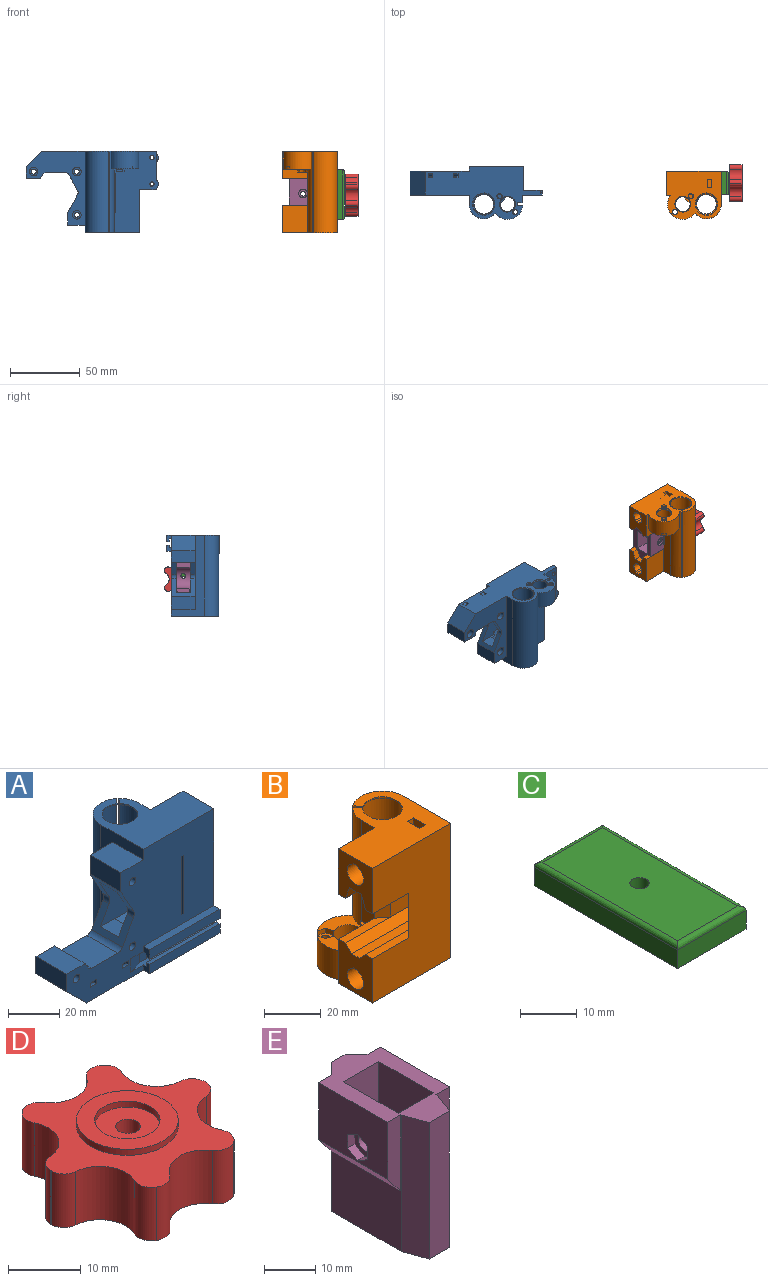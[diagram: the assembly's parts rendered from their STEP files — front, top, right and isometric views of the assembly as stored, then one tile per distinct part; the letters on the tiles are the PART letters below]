
ASSEMBLY  parts=5 mates=4
PART A: 160 faces, bbox 95x38x58 mm
  f0: plane 12.5x7.8mm, normal (1,0,0), area 61.7mm2, adj f1,f4,f8,f146,f148,f149
  f1: plane 19.74x17.5mm, normal (0,0,1), area 118mm2, adj f0,f8,f15,f16,f92,f98,f99,f100
  f2: plane 81.5x58mm, normal (0,-1,0), area 2689.5mm2, adj f3,f4,f30,f31,f32,f33,f34,f35
  f3: plane 58x20.5mm, normal (1,0,0), area 534.3mm2, adj f2,f4,f8,f26,f27,f28,f29,f44
  f4: plane 82.55x38mm, normal (0,0,-1), area 1612.4mm2, adj f0,f2,f3,f8,f16,f23,f43,f45
  f5: plane 2.33x1.17mm, normal (0,0,-1), area 0.6mm2, adj f12,f112,f120
  f6: plane 2.33x1.17mm, normal (0,0,-1), area 0.6mm2, adj f107,f112,f120
  f7: plane 2.33x1.17mm, normal (0,0,-1), area 0.6mm2, adj f107,f110,f120
  f8: plane 58x31.5mm, normal (0,1,0), area 1132.1mm2, adj f0,f1,f3,f4,f9,f44,f48,f49
  f9: plane 45x13.07mm, normal (1,0,0), area 391.3mm2, adj f8,f11,f16,f44,f48,f50,f64,f65
  f10: plane 4.64x4.64mm, normal (0,0,1), area 5.1mm2, adj f105,f114
  f11: plane 0.06x0.03mm, normal (0,0,1), area 0mm2, adj f9,f115,f116
  f12: plane 3.96x3.96mm, normal (0.71,0.71,0), area 4.5mm2, adj f5,f13,f14,f19,f109,f110,f111,f112
  f13: plane 2.33x1.17mm, normal (0,0,-1), area 0.6mm2, adj f12,f110,f120
  f14: plane 3.96x3.96mm, normal (0.71,-0.71,0), area 18.4mm2, adj f12,f18,f95,f96,f106,f107,f109,f111
  f15: cylinder r=5.25mm len=11.6mm, axis (0,0,-1), area 357mm2, adj f1,f17,f18,f94,f95,f97,f102,f103
  f16: cylinder r=10.5mm len=58mm, axis (0,0,-1), area 1765.4mm2, adj f1,f4,f9,f43,f44,f89,f90,f91
  f17: plane 3x0.78mm, normal (-0.53,0.85,0), area 2.8mm2, adj f15,f19,f95,f106
  f18: plane 3x0.78mm, normal (0.85,-0.53,0), area 2.8mm2, adj f14,f15,f95,f106
  f19: plane 3.96x3.96mm, normal (-0.71,0.71,0), area 18.5mm2, adj f12,f17,f95,f96,f106,f107,f109,f113
  f20: cylinder r=1.65mm len=9.5mm, axis (0,0,-1), area 98.5mm2, adj f97,f123
  f21: cylinder r=7.5mm len=56.85mm, axis (0,0,-1), area 2622.3mm2, adj f22,f87,f89,f90,f91
  f22: cone r=7.5mm half-angle=63.4deg, axis (0,0,-1), area 24.9mm2, adj f21,f88,f89,f90
  f23: plane 53x42.5mm, normal (0,1,0), area 903.5mm2, adj f4,f24,f35,f36,f37,f38,f40,f41
  f24: cylinder r=3.5mm len=3.5mm, axis (0,-1,0), area 12.4mm2, adj f23,f38,f40,f65
  f25: plane 10x3.25mm, normal (1,0,0), area 23.1mm2, adj f48,f64,f65,f68,f69,f84
  f26: plane 30.15x0.91mm, normal (0,0.71,-0.71), area 36.2mm2, adj f3,f27,f29,f80,f81
  f27: cylinder r=4.07mm len=29.1mm, axis (1,0,0), area 618.8mm2, adj f3,f26,f28,f81
  f28: plane 30.15x0.91mm, normal (0,-0.71,-0.71), area 36.2mm2, adj f3,f27,f29,f80,f81
  f29: plane 30.11x2.39mm, normal (0,0,-1), area 70.9mm2, adj f3,f26,f28,f80
  f30: plane 28x6.57mm, normal (1,0,0), area 108.5mm2, adj f2,f48,f50,f67,f68,f69
  f31: plane 28x6.57mm, normal (-1,0,0), area 108.5mm2, adj f2,f48,f50,f58,f59,f60
  f32: cylinder r=1.8mm len=13.5mm, axis (0,-1,0), area 152.7mm2, adj f2,f57
  f33: cylinder r=1.8mm len=13.5mm, axis (0,-1,0), area 152.7mm2, adj f2,f55
  f34: cylinder r=1.8mm len=13.5mm, axis (0,-1,0), area 152.7mm2, adj f2,f53
  f35: plane 17x1.73mm, normal (0.5,0,0.87), area 34mm2, adj f2,f23,f36,f51
  f36: plane 17x14.58mm, normal (0,0,1), area 247.8mm2, adj f2,f23,f35,f37
  f37: cylinder r=3mm len=17mm, axis (0,-1,0), area 54.2mm2, adj f2,f23,f36,f38
  f38: plane 17x11.05mm, normal (-0.87,0,0.49), area 116.3mm2, adj f2,f23,f24,f37,f39,f65,f68,f84
  f39: cylinder r=3.5mm len=3.5mm, axis (0,-1,0), area 12.4mm2, adj f2,f38,f40,f68
  f40: plane 17x12.59mm, normal (-0.87,0,-0.49), area 132.8mm2, adj f2,f23,f24,f39,f41,f65,f68,f85
  f41: plane 17x9.14mm, normal (-1,0,0), area 155.4mm2, adj f2,f23,f40,f42
  f42: plane 17x12.5mm, normal (0,0,1), area 212.5mm2, adj f2,f23,f41,f43
  f43: plane 58x23.5mm, normal (-1,0,0), area 462mm2, adj f2,f4,f16,f23,f42,f44
  f44: plane 39x34mm, normal (0,0,1), area 815.2mm2, adj f2,f3,f8,f9,f16,f43,f88,f89
  f45: plane 17x10.95mm, normal (-0.71,0,-0.71), area 263.3mm2, adj f2,f4,f23,f46
  f46: plane 17x8.3mm, normal (-1,0,0), area 141.1mm2, adj f2,f23,f45,f47
  f47: plane 17x10.21mm, normal (0,0,1), area 173.6mm2, adj f2,f23,f46,f51
  f48: plane 41.5x17mm, normal (0,0,1), area 173.3mm2, adj f2,f3,f8,f9,f25,f30,f31,f49
  f49: plane 28x6.57mm, normal (-1,0,0), area 108.5mm2, adj f8,f48,f50,f61,f62,f63
  f50: plane 41.5x17mm, normal (0,0,-1), area 256.4mm2, adj f2,f3,f8,f9,f30,f31,f49,f60
  f51: plane 17x2.97mm, normal (0.87,0,0.5), area 58.3mm2, adj f2,f23,f35,f47
  f52: cylinder r=3.1mm len=6.2mm, axis (0,1,0), area 68.2mm2, adj f23,f53
  f53: plane 6.2x6.2mm, normal (0,1,0), area 20mm2, adj f34,f52
  f54: cylinder r=3.1mm len=6.2mm, axis (0,1,0), area 68.2mm2, adj f23,f55
  f55: plane 6.2x6.2mm, normal (0,1,0), area 20mm2, adj f33,f54
  f56: cylinder r=3.1mm len=6.2mm, axis (0,1,0), area 68.2mm2, adj f23,f57
  f57: plane 6.2x6.2mm, normal (0,1,0), area 20mm2, adj f32,f56
  f58: plane 17x3.07mm, normal (0,0.71,0.71), area 73.8mm2, adj f3,f31,f48,f59
  f59: plane 19.31x17mm, normal (0,1,0), area 328.3mm2, adj f3,f31,f58,f60
  f60: plane 17x5.62mm, normal (0,0.94,-0.34), area 101.7mm2, adj f3,f31,f50,f59
  f61: plane 17x5.62mm, normal (0,-0.94,-0.34), area 101.7mm2, adj f3,f49,f50,f62
  f62: plane 38.38x30.5mm, normal (0,-1,0), area 659.9mm2, adj f3,f4,f49,f61,f63,f150,f151,f152
  f63: plane 17x3.07mm, normal (0,-0.71,0.71), area 73.8mm2, adj f3,f48,f49,f62
  f64: plane 23.5x3.07mm, normal (0,-0.71,0.71), area 102mm2, adj f9,f25,f48,f65
  f65: plane 31.95x22mm, normal (0,-1,0), area 573.5mm2, adj f9,f24,f25,f38,f40,f64,f66,f83
  f66: plane 23.5x5.62mm, normal (0,-0.94,-0.34), area 131.9mm2, adj f9,f50,f65,f70,f83,f85
  f67: plane 23.5x5.62mm, normal (0,0.94,-0.34), area 131.9mm2, adj f30,f50,f68,f70,f85,f86
  f68: plane 31.95x22mm, normal (0,1,0), area 573.5mm2, adj f25,f30,f38,f39,f40,f67,f69,f84
  f69: plane 23.5x3.07mm, normal (0,0.71,0.71), area 102mm2, adj f25,f30,f48,f68
  f70: plane 8.04x2.93mm, normal (1,0,0), area 20.4mm2, adj f50,f66,f67,f85
  f71: plane 30.15x0.91mm, normal (0,0.71,-0.71), area 36.2mm2, adj f3,f72,f74,f76,f77
  f72: cylinder r=4.07mm len=29.1mm, axis (1,0,0), area 618.8mm2, adj f3,f71,f73,f77
  f73: plane 30.15x0.91mm, normal (0,-0.71,-0.71), area 36.2mm2, adj f3,f72,f74,f76,f77
  f74: plane 30.11x2.39mm, normal (0,0,-1), area 70.9mm2, adj f3,f71,f73,f76
  f75: cylinder r=5mm len=10mm, axis (-1,0,0), area 157.1mm2, adj f76,f78
  f76: cone r=5mm half-angle=13.6deg, axis (-1,0,0), area 85.3mm2, adj f71,f73,f74,f75,f77
  f77: plane 8.6x8.3mm, normal (-1,0,0), area 5.1mm2, adj f71,f72,f73,f76
  f78: plane 10x10mm, normal (1,0,0), area 78.5mm2, adj f75
  f79: cylinder r=5mm len=10mm, axis (1,0,0), area 157.1mm2, adj f80,f82
  f80: cone r=5mm half-angle=13.6deg, axis (-1,0,0), area 85.3mm2, adj f26,f28,f29,f79,f81
  f81: plane 8.6x8.3mm, normal (-1,0,0), area 5.1mm2, adj f26,f27,f28,f80
  f82: plane 10x10mm, normal (1,0,0), area 78.5mm2, adj f79
  f83: plane 2.69x0.98mm, normal (-1,0,0), area 1.3mm2, adj f65,f66,f85
  f84: plane 10x7.79mm, normal (0,0,1), area 77.9mm2, adj f25,f38,f65,f68
  f85: plane 11.45x10mm, normal (0,0,-1), area 90.3mm2, adj f40,f65,f66,f67,f68,f70,f83,f86
  f86: plane 2.69x0.98mm, normal (-1,0,0), area 1.3mm2, adj f67,f68,f85
  f87: cone r=7.5mm half-angle=59deg, axis (0,0,-1), area 28.4mm2, adj f4,f21
  f88: cylinder r=7mm len=14mm, axis (0,0,1), area 25.8mm2, adj f22,f44,f89,f90
  f89: plane 57.5x2.69mm, normal (-0.77,0.64,0), area 173.1mm2, adj f16,f21,f22,f44,f88,f91
  f90: plane 57.5x2.69mm, normal (0.77,-0.64,0), area 173.1mm2, adj f16,f21,f22,f44,f88,f91
  f91: plane 2.94x2.7mm, normal (0,0,1), area 3mm2, adj f16,f21,f89,f90
  f92: cylinder r=11mm len=19.74mm, axis (0,0,-1), area 327.5mm2, adj f1,f4,f16,f146
  f93: cylinder r=1.65mm len=8mm, axis (0,0,-1), area 82.9mm2, adj f95,f122
  f94: cone r=5.25mm half-angle=26.6deg, axis (0,0,-1), area 34.6mm2, adj f4,f15
  f95: plane 8.7x8.7mm, normal (0,0,1), area 24.1mm2, adj f14,f15,f17,f18,f19,f93,f96
  f96: plane 3.96x3.96mm, normal (0.71,0.71,0), area 16.8mm2, adj f14,f19,f95,f109
  f97: plane 6.25x6.25mm, normal (0,0,1), area 18.6mm2, adj f15,f20,f98,f99,f100,f101,f102,f103
  f98: plane 3.12x2mm, normal (-0.97,0.26,0), area 6.5mm2, adj f1,f97,f99,f104
  f99: plane 2.29x2.29mm, normal (-0.71,-0.71,0), area 6.5mm2, adj f1,f97,f98,f100
  f100: plane 3.12x2mm, normal (0.26,-0.97,0), area 6.5mm2, adj f1,f97,f99,f101
  f101: plane 3.12x2mm, normal (0.97,-0.26,0), area 6.5mm2, adj f1,f97,f100,f103
  f102: plane 2x0.63mm, normal (0.71,0.71,0), area 1.8mm2, adj f1,f15,f97,f104
  f103: plane 2x0.63mm, normal (0.71,0.71,0), area 1.8mm2, adj f1,f15,f97,f101
  f104: plane 3.12x2mm, normal (-0.26,0.97,0), area 6.5mm2, adj f1,f97,f98,f102
  f105: plane 7.23x7.23mm, normal (0.71,0.71,0), area 13.9mm2, adj f1,f8,f10,f15,f16,f106,f114,f119
  f106: plane 5.89x5.89mm, normal (0,0,-1), area 12.9mm2, adj f14,f15,f17,f18,f19,f105,f107
  f107: plane 3.96x3.96mm, normal (-0.71,-0.71,0), area 4.5mm2, adj f6,f7,f14,f19,f106,f110,f111,f112
  f108: plane 0.06x0.03mm, normal (0,0,1), area 0mm2, adj f8,f117,f118
  f109: plane 4.77x4.77mm, normal (0,0,-1), area 6.4mm2, adj f12,f14,f19,f96
  f110: plane 2.33x2.33mm, normal (0.71,-0.71,0), area 1.6mm2, adj f7,f12,f13,f107,f111
  f111: plane 3.15x3.15mm, normal (0,0,-1), area 3.8mm2, adj f12,f14,f107,f110
  f112: plane 2.33x2.33mm, normal (-0.71,0.71,0), area 1.7mm2, adj f5,f6,f12,f107,f113
  f113: plane 3.15x3.15mm, normal (0,0,-1), area 3.8mm2, adj f12,f19,f107,f112
  f114: cylinder r=5.25mm len=4.64mm, axis (0,0,-1), area 10.6mm2, adj f10,f105,f119
  f115: plane 1.5x0.03mm, normal (-0.71,-0.71,0), area 0.1mm2, adj f9,f11,f116,f119
  f116: plane 1.5x0.03mm, normal (-0.71,0.71,0), area 0.1mm2, adj f9,f11,f115,f119
  f117: plane 1.5x0.03mm, normal (0.71,-0.71,0), area 0.1mm2, adj f8,f108,f118,f119
  f118: plane 1.5x0.03mm, normal (-0.71,-0.71,0), area 0.1mm2, adj f8,f108,f117,f119
  f119: plane 7.23x7.23mm, normal (0,0,1), area 20.8mm2, adj f8,f9,f16,f105,f114,f115,f116,f117
  f120: cylinder r=1.65mm len=3.3mm, axis (0,0,-1), area 10.4mm2, adj f5,f6,f7,f13,f121
  f121: plane 3.3x3.3mm, normal (0,0,-1), area 8.6mm2, adj f120
  f122: cone r=1.65mm half-angle=15.4deg, axis (0,0,-1), area 11.6mm2, adj f4,f93
  f123: cone r=1.65mm half-angle=15.4deg, axis (0,0,-1), area 11.6mm2, adj f4,f20
  f124: plane 4.5x3.5mm, normal (-1,0,0), area 12.8mm2, adj f2,f4,f125,f126,f127,f128
  f125: plane 46x3.8mm, normal (0,0,1), area 155.2mm2, adj f2,f3,f124,f126,f135,f136,f137
  f126: plane 39x2mm, normal (0,1,0), area 78mm2, adj f3,f124,f125,f127
  f127: plane 39x2mm, normal (0,0,1), area 78mm2, adj f3,f124,f126,f128
  f128: plane 39x4.5mm, normal (0,-1,0), area 175.5mm2, adj f3,f4,f124,f127
  f129: plane 4.5x3.5mm, normal (-1,0,0), area 12.8mm2, adj f2,f130,f131,f132,f133,f134
  f130: plane 39x3.5mm, normal (0,0,1), area 136.5mm2, adj f2,f3,f129,f131
  f131: plane 39x4.5mm, normal (0,-1,0), area 175.5mm2, adj f3,f129,f130,f132
  f132: plane 39x2mm, normal (0,0,-1), area 78mm2, adj f3,f129,f131,f133
  f133: plane 39x2mm, normal (0,1,0), area 78mm2, adj f3,f129,f132,f134
  f134: plane 46x3.8mm, normal (0,0,-1), area 155.2mm2, adj f2,f3,f129,f133,f135,f136,f137
  f135: plane 6.5x0.3mm, normal (1,0,0), area 2mm2, adj f125,f134,f136,f137
  f136: plane 39x6.5mm, normal (0,-1,0), area 253.5mm2, adj f3,f125,f134,f135
  f137: plane 7x6.5mm, normal (0.27,-0.96,0), area 47.3mm2, adj f2,f125,f134,f135
  f138: plane 8.6x5.5mm, normal (-1,0,0), area 21.1mm2, adj f2,f4,f139,f141
  f139: cylinder r=3.5mm len=6.6mm, axis (1,0,0), area 32.6mm2, adj f2,f4,f138,f140
  f140: plane 8.6x5.5mm, normal (1,0,0), area 21.1mm2, adj f2,f4,f139,f141
  f141: cylinder r=5.5mm len=8.6mm, axis (1,0,0), area 41.8mm2, adj f2,f4,f138,f140
  f142: cylinder r=3.5mm len=6.6mm, axis (1,0,0), area 32.6mm2, adj f2,f4,f143,f145
  f143: plane 8.6x5.5mm, normal (1,0,0), area 21.1mm2, adj f2,f4,f142,f144
  f144: cylinder r=5.5mm len=8.6mm, axis (1,0,0), area 41.8mm2, adj f2,f4,f143,f145
  f145: plane 8.6x5.5mm, normal (-1,0,0), area 21.1mm2, adj f2,f4,f142,f144
  f146: plane 12.5x3.92mm, normal (0,-1,0), area 49mm2, adj f0,f1,f4,f92
  f147: plane 6.5x5.5mm, normal (1,0,0), area 35.8mm2, adj f4,f8,f148,f149
  f148: plane 5.5x3.5mm, normal (0,0,1), area 19.2mm2, adj f0,f8,f147,f149
  f149: plane 6.5x3.5mm, normal (0,1,0), area 22.7mm2, adj f0,f4,f147,f148
  f150: plane 20.15x3.5mm, normal (1,0,0), area 60.4mm2, adj f4,f8,f62,f151,f155,f157
  f151: cylinder r=4.5mm len=6.71mm, axis (0,1,0), area 11.4mm2, adj f62,f150,f157
  f152: plane 12x3.5mm, normal (0,0,1), area 42mm2, adj f3,f8,f62,f153
  f153: plane 3.5x0.65mm, normal (1,0,0), area 2.3mm2, adj f8,f62,f152,f155
  f154: cylinder r=1.4mm len=3.35mm, axis (0,1,0), area 29.5mm2, adj f62,f158
  f155: cylinder r=4.5mm len=6.71mm, axis (0,1,0), area 26.5mm2, adj f8,f62,f150,f153
  f156: cylinder r=1.4mm len=3.35mm, axis (0,1,0), area 29.5mm2, adj f62,f159
  f157: plane 6.71x1.5mm, normal (0,1,0), area 7mm2, adj f150,f151
  f158: cone r=1.4mm half-angle=45deg, axis (0,1,0), area 2mm2, adj f8,f154
  f159: cone r=1.55mm half-angle=45deg, axis (0,1,0), area 2mm2, adj f8,f156
PART B: 111 faces, bbox 39x34.5x58 mm
  f0: plane 2.33x1.17mm, normal (0,0,-1), area 0.6mm2, adj f4,f99,f107
  f1: plane 2.33x1.17mm, normal (0,0,-1), area 0.6mm2, adj f4,f97,f107
  f2: plane 2.33x1.17mm, normal (0,0,-1), area 0.6mm2, adj f95,f97,f107
  f3: plane 2.33x1.17mm, normal (0,0,-1), area 0.6mm2, adj f95,f99,f107
  f4: plane 3.96x3.96mm, normal (-0.71,0.71,0), area 4.5mm2, adj f0,f1,f5,f11,f96,f97,f98,f99
  f5: plane 3.96x3.96mm, normal (0.71,0.71,0), area 18.5mm2, adj f4,f10,f82,f83,f94,f95,f96,f100
  f6: cylinder r=5.25mm len=11.6mm, axis (0,0,-1), area 357mm2, adj f7,f10,f12,f81,f82,f84,f90,f91
  f7: plane 19.82x17.5mm, normal (0,0,1), area 144.7mm2, adj f6,f8,f9,f80,f85,f86,f87,f88
  f8: plane 19.07x18mm, normal (0,1,0), area 136.7mm2, adj f7,f13,f27,f36,f66,f80,f92,f101
  f9: cylinder r=10.5mm len=58mm, axis (0,0,1), area 1765.4mm2, adj f7,f13,f33,f36,f38,f77,f78,f79
  f10: plane 3x0.78mm, normal (0.53,0.85,0), area 2.8mm2, adj f5,f6,f82,f94
  f11: plane 3.96x3.96mm, normal (-0.71,-0.71,0), area 18.4mm2, adj f4,f12,f82,f83,f94,f95,f96,f98
  f12: plane 3x0.78mm, normal (-0.85,-0.53,0), area 2.8mm2, adj f6,f11,f82,f94
  f13: plane 43.5x6.5mm, normal (-1,0,0), area 282.8mm2, adj f8,f9,f26,f38,f67,f101
  f14: cylinder r=7mm len=14mm, axis (0,0,1), area 25.8mm2, adj f38,f40,f78,f79
  f15: cylinder r=1.7mm len=3.4mm, axis (1,0,0), area 16mm2, adj f44,f73
  f16: plane 20.02x0.89mm, normal (0,0.71,-0.71), area 24.3mm2, adj f17,f19,f31,f61,f74,f76
  f17: plane 20x2.39mm, normal (0,0,-1), area 47.6mm2, adj f16,f18,f20,f31,f61,f74
  f18: plane 20.02x0.89mm, normal (0,-0.71,-0.71), area 24.3mm2, adj f17,f19,f20,f31,f74,f76
  f19: cylinder r=4.07mm len=19.6mm, axis (-1,0,0), area 416.8mm2, adj f16,f18,f31,f76
  f20: plane 0.46x0.12mm, normal (-1,0,0), area 0mm2, adj f17,f18,f74
  f21: cylinder r=4.07mm len=19.6mm, axis (-1,0,0), area 416.8mm2, adj f22,f24,f27,f69
  f22: plane 20.02x0.89mm, normal (0,0.71,-0.71), area 24.3mm2, adj f21,f23,f27,f62,f69,f72
  f23: plane 20x2.39mm, normal (0,0,-1), area 47.6mm2, adj f22,f24,f25,f27,f62,f72
  f24: plane 20.02x0.89mm, normal (0,-0.71,-0.71), area 24.3mm2, adj f21,f23,f25,f27,f69,f72
  f25: plane 0.46x0.12mm, normal (-1,0,0), area 0mm2, adj f23,f24,f72
  f26: plane 19.62x18mm, normal (0,1,0), area 353.1mm2, adj f13,f31,f38,f65
  f27: plane 19.07x17mm, normal (-1,0,0), area 249.5mm2, adj f8,f21,f22,f23,f24,f28,f36,f51
  f28: plane 58x39mm, normal (0,-1,0), area 1914.4mm2, adj f27,f31,f33,f36,f38,f63,f64,f68
  f29: plane 19.31x16.5mm, normal (0,-1,0), area 318.6mm2, adj f33,f52,f53,f67
  f30: plane 19.31x16.5mm, normal (0,1,0), area 318.6mm2, adj f33,f55,f56,f68
  f31: plane 19.62x17mm, normal (-1,0,0), area 235.4mm2, adj f16,f17,f18,f19,f26,f28,f38,f53
  f32: cylinder r=1.7mm len=3.4mm, axis (1,0,0), area 16mm2, adj f48,f71
  f33: plane 58x23.5mm, normal (1,0,0), area 1047.4mm2, adj f9,f28,f29,f30,f36,f38,f51,f52
  f34: cylinder r=1.7mm len=4mm, axis (1,0,0), area 42.7mm2, adj f46,f60
  f35: cylinder r=1.7mm len=4mm, axis (1,0,0), area 42.7mm2, adj f42,f58
  f36: plane 39x34.5mm, normal (0,0,-1), area 907.5mm2, adj f8,f9,f27,f28,f33,f39,f46,f47
  f37: cylinder r=7.5mm len=56.85mm, axis (0,0,1), area 2622.3mm2, adj f39,f40,f77,f78,f79
  f38: plane 39x34mm, normal (0,0,1), area 797.2mm2, adj f9,f13,f14,f26,f28,f31,f33,f41
  f39: cone r=8mm half-angle=59deg, axis (0,0,-1), area 28.4mm2, adj f36,f37
  f40: cone r=7.5mm half-angle=63.4deg, axis (0,0,-1), area 24.9mm2, adj f14,f37,f78,f79
  f41: plane 10.6x3mm, normal (0,-1,0), area 31.8mm2, adj f38,f42,f44,f45
  f42: plane 10.6x6mm, normal (-1,0,0), area 54.5mm2, adj f35,f38,f41,f43,f45
  f43: plane 10.6x3mm, normal (0,1,0), area 31.8mm2, adj f38,f42,f44,f45
  f44: plane 10.6x6mm, normal (1,0,0), area 54.5mm2, adj f15,f38,f41,f43,f45
  f45: plane 6x3mm, normal (0,0,1), area 18mm2, adj f41,f42,f43,f44
  f46: plane 9.1x6mm, normal (-1,0,0), area 45.5mm2, adj f34,f36,f47,f49,f50
  f47: plane 9.1x3mm, normal (0,1,0), area 27.3mm2, adj f36,f46,f48,f50
  f48: plane 9.1x6mm, normal (1,0,0), area 45.5mm2, adj f32,f36,f47,f49,f50
  f49: plane 9.1x3mm, normal (0,-1,0), area 27.3mm2, adj f36,f46,f48,f50
  f50: plane 6x3mm, normal (0,0,-1), area 18mm2, adj f46,f47,f48,f49
  f51: plane 39x3.86mm, normal (0,0,1), area 150.5mm2, adj f27,f33,f52,f56
  f52: plane 39x3.07mm, normal (0,-0.71,0.71), area 169.4mm2, adj f27,f29,f33,f51,f66
  f53: plane 39x5.62mm, normal (0,-0.94,-0.34), area 233.2mm2, adj f29,f31,f33,f54,f65
  f54: plane 39x5.91mm, normal (0,0,-1), area 230.5mm2, adj f31,f33,f53,f55
  f55: plane 39x5.62mm, normal (0,0.94,-0.34), area 233.2mm2, adj f30,f31,f33,f54,f64
  f56: plane 39x3.07mm, normal (0,0.71,0.71), area 169.4mm2, adj f27,f30,f33,f51,f63
  f57: cylinder r=3mm len=6mm, axis (1,0,0), area 56.5mm2, adj f33,f58
  f58: plane 6x6mm, normal (1,0,0), area 19.2mm2, adj f35,f57
  f59: cylinder r=3mm len=6mm, axis (1,0,0), area 56.5mm2, adj f33,f60
  f60: plane 6x6mm, normal (1,0,0), area 19.2mm2, adj f34,f59
  f61: plane 0.46x0.12mm, normal (-1,0,0), area 0mm2, adj f16,f17,f74
  f62: plane 0.46x0.12mm, normal (-1,0,0), area 0mm2, adj f22,f23,f72
  f63: plane 22.5x3.5mm, normal (0,0,1), area 70.9mm2, adj f27,f28,f56,f68
  f64: plane 22.5x3.5mm, normal (0,0,-1), area 70.9mm2, adj f28,f31,f55,f68
  f65: plane 22.5x3.5mm, normal (0,0,-1), area 70.9mm2, adj f26,f31,f53,f67
  f66: plane 22.5x3.5mm, normal (0,0,1), area 70.9mm2, adj f8,f27,f52,f67
  f67: plane 19.31x4.5mm, normal (-0.61,-0.79,0), area 110.1mm2, adj f13,f29,f65,f66
  f68: plane 19.31x4.5mm, normal (-0.61,0.79,0), area 110.1mm2, adj f28,f30,f63,f64
  f69: plane 8.6x8.3mm, normal (1,0,0), area 5.1mm2, adj f21,f22,f24,f72
  f70: cylinder r=5.5mm len=11mm, axis (-1,0,0), area 172.8mm2, adj f71,f72
  f71: plane 11x11mm, normal (-1,0,0), area 86mm2, adj f32,f70
  f72: cone r=5.5mm half-angle=22.5deg, axis (1,0,0), area 95.6mm2, adj f22,f23,f24,f25,f62,f69,f70
  f73: plane 11x11mm, normal (-1,0,0), area 86mm2, adj f15,f75
  f74: cone r=5.5mm half-angle=22.5deg, axis (1,0,0), area 95.6mm2, adj f16,f17,f18,f20,f61,f75,f76
  f75: cylinder r=5.5mm len=11mm, axis (-1,0,0), area 172.8mm2, adj f73,f74
  f76: plane 8.6x8.3mm, normal (1,0,0), area 5.1mm2, adj f16,f18,f19,f74
  f77: plane 2.94x2.7mm, normal (0,0,1), area 3mm2, adj f9,f37,f78,f79
  f78: plane 57.5x2.69mm, normal (0.77,0.64,0), area 173.1mm2, adj f9,f14,f37,f38,f40,f77
  f79: plane 57.5x2.69mm, normal (-0.77,-0.64,0), area 173.1mm2, adj f9,f14,f37,f38,f40,f77
  f80: cylinder r=11mm len=19.82mm, axis (0,0,-1), area 430.8mm2, adj f7,f8,f9,f36
  f81: cone r=5.25mm half-angle=26.6deg, axis (0,0,-1), area 34.6mm2, adj f6,f36
  f82: plane 8.7x8.7mm, normal (0,0,1), area 24.1mm2, adj f5,f6,f10,f11,f12,f83,f106
  f83: plane 3.96x3.96mm, normal (-0.71,0.71,0), area 16.8mm2, adj f5,f11,f82,f96
  f84: plane 6.25x6.25mm, normal (0,0,1), area 18.6mm2, adj f6,f85,f86,f87,f88,f89,f90,f91
  f85: plane 3.12x2mm, normal (-0.97,-0.26,0), area 6.5mm2, adj f7,f84,f86,f90
  f86: plane 3.12x2mm, normal (-0.26,-0.97,0), area 6.5mm2, adj f7,f84,f85,f87
  f87: plane 2.29x2.29mm, normal (0.71,-0.71,0), area 6.5mm2, adj f7,f84,f86,f88
  f88: plane 3.12x2mm, normal (0.97,0.26,0), area 6.5mm2, adj f7,f84,f87,f89
  f89: plane 3.12x2mm, normal (0.26,0.97,0), area 6.5mm2, adj f7,f84,f88,f91
  f90: plane 2x0.63mm, normal (-0.71,0.71,0), area 1.8mm2, adj f6,f7,f84,f85
  f91: plane 2x0.63mm, normal (-0.71,0.71,0), area 1.8mm2, adj f6,f7,f84,f89
  f92: plane 7.23x7.23mm, normal (-0.71,0.71,0), area 13.9mm2, adj f6,f7,f8,f9,f93,f94,f101,f102
  f93: plane 4.64x4.64mm, normal (0,0,1), area 5.1mm2, adj f92,f102,f103,f104
  f94: plane 5.89x5.89mm, normal (0,0,-1), area 12.9mm2, adj f5,f6,f10,f11,f12,f92,f95
  f95: plane 3.96x3.96mm, normal (0.71,-0.71,0), area 4.5mm2, adj f2,f3,f5,f11,f94,f97,f98,f99
  f96: plane 4.77x4.77mm, normal (0,0,-1), area 6.4mm2, adj f4,f5,f11,f83
  f97: plane 2.33x2.33mm, normal (-0.71,-0.71,0), area 1.6mm2, adj f1,f2,f4,f95,f98
  f98: plane 3.15x3.15mm, normal (0,0,-1), area 3.8mm2, adj f4,f11,f95,f97
  f99: plane 2.33x2.33mm, normal (0.71,0.71,0), area 1.7mm2, adj f0,f3,f4,f95,f100
  f100: plane 3.15x3.15mm, normal (0,0,-1), area 3.8mm2, adj f4,f5,f95,f99
  f101: plane 7.23x7.23mm, normal (0,0,1), area 20.8mm2, adj f8,f9,f13,f92,f102,f103,f104
  f102: cylinder r=5.25mm len=2.59mm, axis (0,0,-1), area 4.2mm2, adj f92,f93,f101,f103
  f103: plane 1.5x1.02mm, normal (-0.71,0.71,0), area 2.2mm2, adj f93,f101,f102,f104
  f104: cylinder r=5.25mm len=2.59mm, axis (0,0,-1), area 4.2mm2, adj f92,f93,f101,f103
  f105: cylinder r=1.65mm len=9.5mm, axis (0,0,-1), area 98.5mm2, adj f84,f110
  f106: cylinder r=1.65mm len=8mm, axis (0,0,-1), area 82.9mm2, adj f82,f109
  f107: cylinder r=1.65mm len=3.3mm, axis (0,0,-1), area 10.4mm2, adj f0,f1,f2,f3,f108
  f108: plane 3.3x3.3mm, normal (0,0,-1), area 8.6mm2, adj f107
  f109: cone r=1.65mm half-angle=15.4deg, axis (0,0,-1), area 11.6mm2, adj f36,f106
  f110: cone r=1.65mm half-angle=15.4deg, axis (0,0,-1), area 11.6mm2, adj f36,f105
PART C: 20 faces, bbox 18.7x39.3x6.5 mm
  f0: plane 3.74x1.5mm, normal (0,1,0), area 5.6mm2, adj f1,f8,f9,f10
  f1: plane 2.98x2.98mm, normal (-0.71,0.71,0), area 6.3mm2, adj f0,f2,f9,f10
  f2: plane 19.22x1.5mm, normal (-1,0,0), area 28.8mm2, adj f1,f3,f9,f10
  f3: plane 5.5x2mm, normal (-0.94,-0.34,0), area 8.8mm2, adj f2,f4,f9,f10
  f4: plane 5.7x1.5mm, normal (0,-1,0), area 8.5mm2, adj f3,f5,f9,f10
  f5: plane 5.5x2mm, normal (0.94,-0.34,0), area 8.8mm2, adj f4,f6,f9,f10
  f6: plane 19.22x1.5mm, normal (1,0,0), area 28.8mm2, adj f5,f8,f9,f10
  f7: cylinder r=1.7mm len=6.5mm, axis (0,0,1), area 69.4mm2, adj f9,f15
  f8: plane 2.98x2.98mm, normal (0.71,0.71,0), area 6.3mm2, adj f0,f6,f9,f10
  f9: plane 27.7x9.7mm, normal (0,0,-1), area 239.7mm2, adj f0,f1,f2,f3,f4,f5,f6,f7
  f10: plane 35.7x17mm, normal (0,0,-1), area 358.1mm2, adj f0,f1,f2,f3,f4,f5,f6,f8
  f11: plane 17x4mm, normal (0,-1,0), area 68mm2, adj f10,f12,f14,f18
  f12: plane 35.7x4mm, normal (1,0,0), area 142.8mm2, adj f10,f11,f13,f16
  f13: plane 17x4mm, normal (0,1,0), area 68mm2, adj f10,f12,f14,f17
  f14: plane 35.7x4mm, normal (-1,0,0), area 142.8mm2, adj f10,f11,f13,f19
  f15: plane 33.7x15mm, normal (0,0,1), area 496.4mm2, adj f7,f16,f17,f18,f19
  f16: bspline ~39.27x1mm, area 56.8mm2, adj f12,f15,f17,f18
  f17: bspline ~18.7x1mm, area 26.5mm2, adj f13,f15,f16,f19
  f18: bspline ~18.7x1mm, area 26.5mm2, adj f11,f15,f16,f19
  f19: bspline ~39.27x1mm, area 56.8mm2, adj f14,f15,f17,f18
PART D: 38 faces, bbox 30x26.7x10 mm
  f0: plane 9x9mm, normal (0,0,1), area 54.5mm2, adj f13,f35
  f1: cylinder r=5mm len=9mm, axis (0,0,-1), area 88.2mm2, adj f14,f15,f23,f34
  f2: cylinder r=15mm len=9mm, axis (0,0,-1), area 0.6mm2, adj f14,f15,f23,f24
  f3: cylinder r=5mm len=9mm, axis (0,0,-1), area 88.4mm2, adj f14,f15,f24,f25
  f4: cylinder r=15mm len=9mm, axis (0,0,-1), area 0.6mm2, adj f14,f15,f25,f26
  f5: cylinder r=5mm len=9mm, axis (0,0,-1), area 88.2mm2, adj f14,f15,f26,f27
  f6: cylinder r=15mm len=9mm, axis (0,0,-1), area 0.6mm2, adj f14,f15,f27,f28
  f7: cylinder r=5mm len=9mm, axis (0,0,-1), area 88mm2, adj f14,f15,f28,f29
  f8: cylinder r=15mm len=9mm, axis (0,0,-1), area 0.7mm2, adj f14,f15,f29,f30
  f9: cylinder r=5mm len=9mm, axis (0,0,-1), area 87.8mm2, adj f14,f15,f30,f31
  f10: cylinder r=15mm len=9mm, axis (0,0,-1), area 0.7mm2, adj f14,f15,f31,f32
  f11: cylinder r=5mm len=9mm, axis (0,0,-1), area 88mm2, adj f14,f15,f32,f33
  f12: cylinder r=15mm len=9mm, axis (0,0,-1), area 0.6mm2, adj f14,f15,f33,f34
  f13: cylinder r=1.7mm len=6.5mm, axis (0,0,-1), area 69.4mm2, adj f0,f22
  f14: plane 30x26.68mm, normal (0,0,1), area 319.8mm2, adj f1,f2,f3,f4,f5,f6,f7,f8
  f15: plane 30x26.68mm, normal (0,0,-1), area 448.5mm2, adj f1,f2,f3,f4,f5,f6,f7,f8
  f16: plane 3.12x2.5mm, normal (0,-1,0), area 7.8mm2, adj f15,f17,f21,f22
  f17: plane 2.7x2.5mm, normal (0.87,-0.5,0), area 7.8mm2, adj f15,f16,f18,f22
  f18: plane 2.7x2.5mm, normal (0.87,0.5,0), area 7.8mm2, adj f15,f17,f19,f22
  f19: plane 3.12x2.5mm, normal (0,1,0), area 7.8mm2, adj f15,f18,f20,f22
  f20: plane 2.7x2.5mm, normal (-0.87,0.5,0), area 7.8mm2, adj f15,f19,f21,f22
  f21: plane 2.7x2.5mm, normal (-0.87,-0.5,0), area 7.8mm2, adj f15,f16,f20,f22
  f22: plane 6.24x5.4mm, normal (0,0,-1), area 16.2mm2, adj f13,f16,f17,f18,f19,f20,f21
  f23: cylinder r=2.5mm len=9mm, axis (0,0,1), area 33.8mm2, adj f1,f2,f14,f15
  f24: cylinder r=2.5mm len=9mm, axis (0,0,1), area 33.8mm2, adj f2,f3,f14,f15
  f25: cylinder r=2.5mm len=9mm, axis (0,0,1), area 33.8mm2, adj f3,f4,f14,f15
  f26: cylinder r=2.5mm len=9mm, axis (0,0,1), area 33.8mm2, adj f4,f5,f14,f15
  f27: cylinder r=2.5mm len=9mm, axis (0,0,1), area 33.8mm2, adj f5,f6,f14,f15
  f28: cylinder r=2.5mm len=9mm, axis (0,0,1), area 33.7mm2, adj f6,f7,f14,f15
  f29: cylinder r=2.5mm len=9mm, axis (0,0,1), area 33.7mm2, adj f7,f8,f14,f15
  f30: cylinder r=2.5mm len=9mm, axis (0,0,1), area 33.7mm2, adj f8,f9,f14,f15
  f31: cylinder r=2.5mm len=9mm, axis (0,0,1), area 33.7mm2, adj f9,f10,f14,f15
  f32: cylinder r=2.5mm len=9mm, axis (0,0,1), area 33.7mm2, adj f10,f11,f14,f15
  f33: cylinder r=2.5mm len=9mm, axis (0,0,1), area 33.7mm2, adj f11,f12,f14,f15
  f34: cylinder r=2.5mm len=9mm, axis (0,0,1), area 33.8mm2, adj f1,f12,f14,f15
  f35: cylinder r=4.5mm len=9mm, axis (0,0,-1), area 28.3mm2, adj f0,f37
  f36: cylinder r=7mm len=14mm, axis (0,0,-1), area 44mm2, adj f14,f37
  f37: plane 14x14mm, normal (0,0,1), area 90.3mm2, adj f35,f36
PART E: 44 faces, bbox 17x27.9x32.6 mm
  f0: plane 19.01x13.55mm, normal (-1,0,0), area 231.4mm2, adj f2,f3,f4,f5,f6,f7,f8,f9
  f1: cylinder r=1.8mm len=3.6mm, axis (1,0,0), area 18.7mm2, adj f12,f40
  f2: plane 18.05x3.65mm, normal (0,1,0), area 58mm2, adj f0,f4,f5,f22,f41
  f3: plane 18.05x3.65mm, normal (0,-1,0), area 58mm2, adj f0,f4,f5,f22,f41
  f4: plane 27.85x17mm, normal (0,0,1), area 242.9mm2, adj f0,f2,f3,f14,f15,f16,f22,f23
  f5: plane 19.01x4.5mm, normal (-0.79,0,-0.61), area 108.4mm2, adj f0,f2,f3,f41
  f6: plane 2.74x2mm, normal (0,0.5,-0.86), area 6.4mm2, adj f0,f7,f11,f12
  f7: plane 2.76x2mm, normal (0,-0.5,-0.87), area 6.4mm2, adj f0,f6,f8,f12
  f8: plane 3.18x2mm, normal (0,-1,-0.01), area 6.4mm2, adj f0,f7,f9,f12
  f9: plane 2.74x2mm, normal (0,-0.5,0.86), area 6.4mm2, adj f0,f8,f10,f12
  f10: plane 2.76x2mm, normal (0,0.5,0.87), area 6.4mm2, adj f0,f9,f11,f12
  f11: plane 3.18x2mm, normal (0,1,0.01), area 6.4mm2, adj f0,f6,f10,f12
  f12: plane 6.35x5.52mm, normal (-1,0,0), area 16mm2, adj f1,f6,f7,f8,f9,f10,f11
  f13: plane 19.01x4.5mm, normal (0.79,0,-0.61), area 68.7mm2, adj f14,f15,f16,f20,f21,f43
  f14: plane 18.05x3.65mm, normal (0,1,0), area 58mm2, adj f4,f13,f16,f23,f43
  f15: plane 18.05x3.65mm, normal (0,-1,0), area 58mm2, adj f4,f13,f16,f23,f43
  f16: plane 19.01x13.55mm, normal (1,0,0), area 227.4mm2, adj f4,f13,f14,f15,f19
  f17: cylinder r=1.8mm len=3.6mm, axis (1,0,0), area 18.7mm2, adj f18,f42
  f18: plane 6.2x6.2mm, normal (1,0,0), area 20mm2, adj f17,f19
  f19: cylinder r=3.1mm len=6.2mm, axis (1,0,0), area 39mm2, adj f16,f18
  f20: plane 12.69x3.26mm, normal (0,0,-1), area 41.4mm2, adj f13,f21,f42
  f21: cylinder r=7.5mm len=15mm, axis (-1,0,0), area 241.6mm2, adj f13,f20,f24,f38,f39,f40,f42
  f22: plane 32.55x19.22mm, normal (-1,0,0), area 282.5mm2, adj f2,f3,f4,f26,f27,f32,f41
  f23: plane 32.55x19.22mm, normal (1,0,0), area 269.5mm2, adj f4,f14,f15,f29,f31,f32,f33,f34
  f24: cylinder r=1.7mm len=7.27mm, axis (0,0,1), area 73.3mm2, adj f21,f33
  f25: plane 32.55x3.74mm, normal (0,1,0), area 121.6mm2, adj f4,f26,f31,f32
  f26: plane 32.55x2.98mm, normal (-0.71,0.71,0), area 137.3mm2, adj f4,f22,f25,f32
  f27: plane 32.55x5.65mm, normal (-0.94,-0.34,0), area 195.6mm2, adj f4,f22,f28,f32
  f28: plane 32.55x5.59mm, normal (0,-1,0), area 182mm2, adj f4,f27,f29,f32
  f29: plane 32.55x5.65mm, normal (0.94,-0.34,0), area 195.6mm2, adj f4,f23,f28,f32
  f30: cylinder r=1.7mm len=6mm, axis (0,0,1), area 64.1mm2, adj f32,f34
  f31: plane 32.55x2.98mm, normal (0.71,0.71,0), area 137.3mm2, adj f4,f23,f25,f32
  f32: plane 27.85x9.7mm, normal (0,0,-1), area 240.6mm2, adj f22,f23,f25,f26,f27,f28,f29,f30
  f33: plane 8x5.55mm, normal (0,0,-1), area 35.3mm2, adj f23,f24,f35,f36,f37
  f34: plane 8x5.55mm, normal (0,0,1), area 35.3mm2, adj f23,f30,f35,f36,f37
  f35: plane 8x2.35mm, normal (0,1,0), area 18.8mm2, adj f23,f33,f34,f37
  f36: plane 8x2.35mm, normal (0,-1,0), area 18.8mm2, adj f23,f33,f34,f37
  f37: plane 5.55x2.35mm, normal (1,0,0), area 13mm2, adj f33,f34,f35,f36
  f38: plane 10.05x9.7mm, normal (0,1,0), area 97.5mm2, adj f4,f21,f40,f42
  f39: plane 10.05x9.7mm, normal (0,-1,0), area 97.5mm2, adj f4,f21,f40,f42
  f40: plane 17.55x15mm, normal (1,0,0), area 228.9mm2, adj f1,f4,f21,f38,f39
  f41: plane 19.01x0.15mm, normal (0,0,-1), area 2.9mm2, adj f2,f3,f5,f22
  f42: plane 15x14.05mm, normal (-1,0,0), area 197.6mm2, adj f4,f17,f20,f21,f38,f39
  f43: plane 19.01x0.15mm, normal (0,0,-1), area 2.9mm2, adj f13,f14,f15,f23
PLACE A rot(axis=(1,0,0),180deg) t=(74.01,23.38,136.47)mm
PLACE B rot(axis=(1,0,0),180deg) t=(225.99,46.88,168.68)mm
PLACE C rot(axis=(-0.58,0.58,-0.58),120deg) t=(251.55,15,79.99)mm
PLACE D rot(axis=(-0.71,0,0.71),180deg) t=(266.55,14.88,79.55)mm
PLACE E rot(axis=(0.58,-0.58,-0.58),120deg) t=(235.1,14.88,81.9)mm
MATE fastened C.f7 <-> D.f36  axis (1,0,0) through (256.55,14.88,79.55)mm
MATE slider E.f4 <-> B.f27  axis (-1,0,0) through (217.05,14.88,94.48)mm
MATE fastened C.f10 <-> B.f33  axis (-1,0,0) through (251.55,14.88,94.68)mm
MATE fastened A.f87 <-> B.f36  axis (0,0,1) through (81.05,-0.12,110.68)mm
